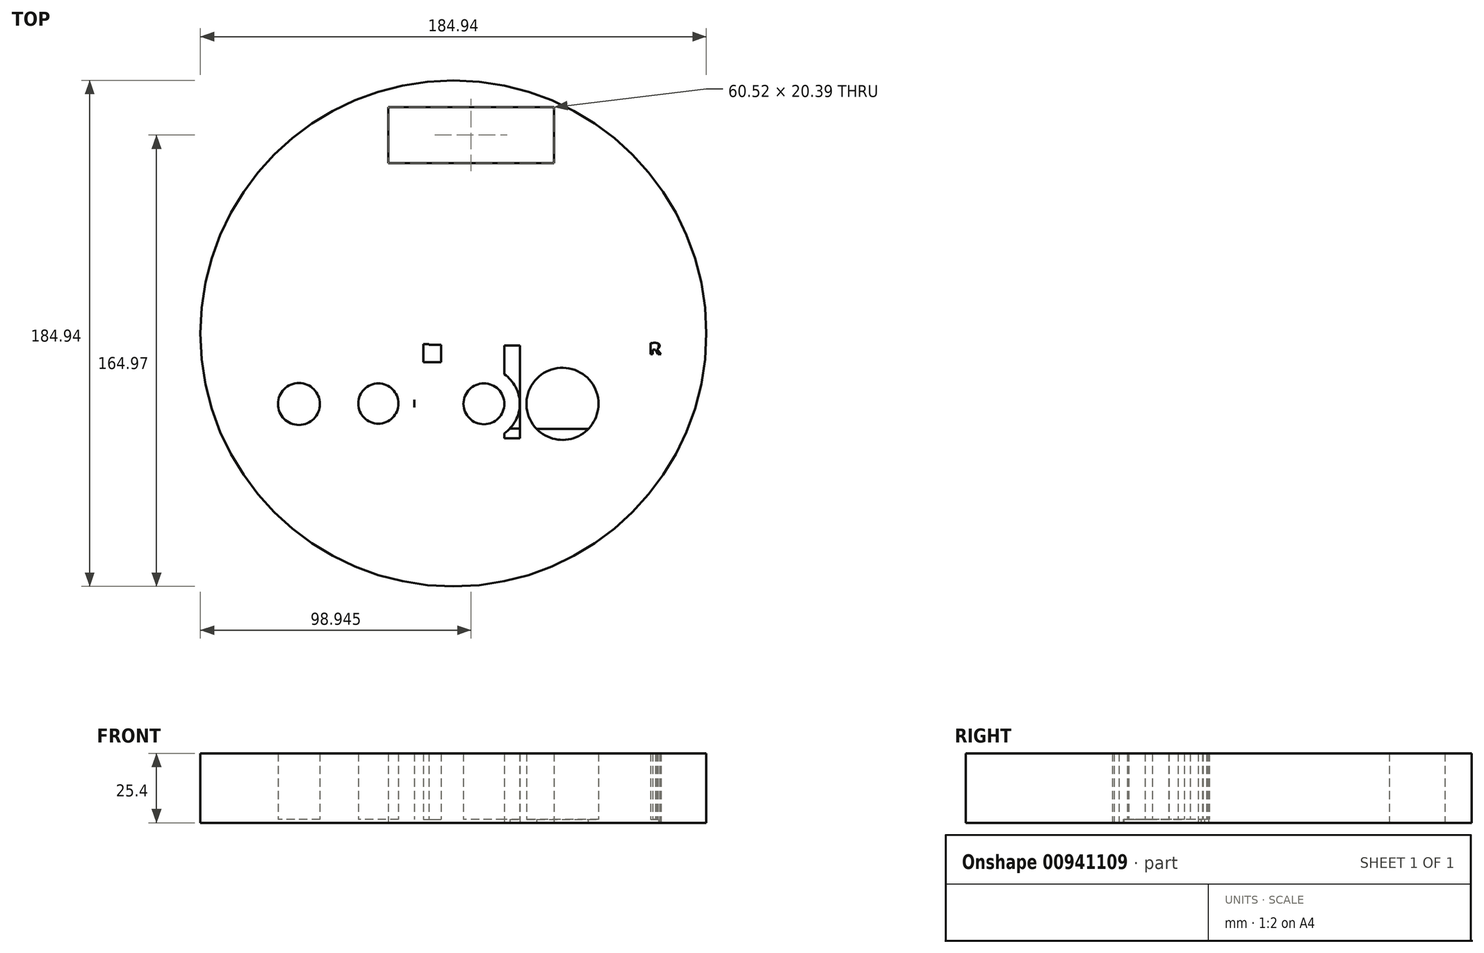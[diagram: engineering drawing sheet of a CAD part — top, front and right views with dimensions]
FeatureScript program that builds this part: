
annotation { "Feature Type Name" : "Feature", "Feature Type Description" : "" }
export const myFeature = defineFeature(function(context is Context, id is Id, definition is map)
    precondition{}
    {
        {
            var Q0;
            Q0=qCreatedBy(makeId("Top.planeOp"),FACE);
            var sketch = newSketch(context, id + "F0", { "sketchPlane" : qUnion([Q0])});
            skLineSegment(sketch, "E0", {"start": v(-100.25, 14.04) * mm, "end": v(-97.31, 8.86) * mm});
            skLineSegment(sketch, "E1", {"start": v(-97.31, 8.86) * mm, "end": v(-67.93, 8.86) * mm});
            skLineSegment(sketch, "E2", {"start": v(-68.34, 8.8) * mm, "end": v(-78.7, 26.94) * mm});
            skLineSegment(sketch, "E3", {"start": v(-78.7, 26.94) * mm, "end": v(-100.25, 14.04) * mm});
            skLineSegment(sketch, "E4", {"start": v(-74.15, 36.69) * mm, "end": v(-57.21, 8.86) * mm});
            skLineSegment(sketch, "E5", {"start": v(-57.21, 9.2) * mm, "end": v(-28.35, 8.86) * mm});
            skLineSegment(sketch, "E6", {"start": v(-28.35, 8.86) * mm, "end": v(-52.72, 50) * mm});
            skLineSegment(sketch, "E7", {"start": v(-52.72, 50) * mm, "end": v(-74.15, 36.69) * mm});
            skLineSegment(sketch, "E8", {"start": v(-26.97, 72.64) * mm, "end": v(-47.88, 60.02) * mm});
            skLineSegment(sketch, "E9", {"start": v(-47.88, 60.02) * mm, "end": v(-17.16, 9.1) * mm});
            skLineSegment(sketch, "E10", {"start": v(-17.46, 9.2) * mm, "end": v(11.36, 8.97) * mm});
            skLineSegment(sketch, "E11", {"start": v(11.36, 8.97) * mm, "end": v(-26.97, 72.64) * mm});
            skCircle(sketch, "E12", {"center": v(-102.75, -12.72) * mm, "radius": 13.23 * mm});
            skCircle(sketch, "E13", {"center": v(-102.75, -12.72) * mm, "radius": 7.67 * mm});
            skCircle(sketch, "E14", {"center": v(-73.71, -12.55) * mm, "radius": 13.19 * mm});
            skCircle(sketch, "E15", {"center": v(-73.71, -12.55) * mm, "radius": 7.35 * mm});
            skLineSegment(sketch, "E16", {"start": v(-95.55, 0.06) * mm, "end": v(-95.55, -24.87) * mm});
            skLineSegment(sketch, "E17", {"start": v(-95.55, -24.87) * mm, "end": v(-89.4, -24.87) * mm});
            skLineSegment(sketch, "E18", {"start": v(-89.4, -24.87) * mm, "end": v(-89.4, 0.06) * mm});
            skLineSegment(sketch, "E19", {"start": v(-95.55, 0.06) * mm, "end": v(-89.4, 0.06) * mm});
            skLineSegment(sketch, "E20.bottom", {"start": v(-66.38, 8.73) * mm, "end": v(-60.6, 8.73) * mm});
            skLineSegment(sketch, "E20.top", {"start": v(-66.38, -25.23) * mm, "end": v(-60.6, -25.23) * mm});
            skLineSegment(sketch, "E20.left", {"start": v(-66.38, 8.73) * mm, "end": v(-66.38, -25.23) * mm});
            skLineSegment(sketch, "E20.right", {"start": v(-60.6, 8.73) * mm, "end": v(-60.6, -25.23) * mm});
            skLineSegment(sketch, "E21.bottom", {"start": v(-57.17, 0.69) * mm, "end": v(-50.84, 0.69) * mm});
            skLineSegment(sketch, "E21.top", {"start": v(-57.17, -24.96) * mm, "end": v(-50.84, -24.96) * mm});
            skLineSegment(sketch, "E21.left", {"start": v(-57.17, 0.69) * mm, "end": v(-57.17, -24.96) * mm});
            skLineSegment(sketch, "E21.right", {"start": v(-50.84, 0.69) * mm, "end": v(-50.84, -24.96) * mm});
            skLineSegment(sketch, "E22.bottom", {"start": v(-57.21, 8.86) * mm, "end": v(-50.84, 8.86) * mm});
            skLineSegment(sketch, "E22.top", {"start": v(-57.21, 2.59) * mm, "end": v(-50.84, 2.59) * mm});
            skLineSegment(sketch, "E22.left", {"start": v(-57.21, 8.86) * mm, "end": v(-57.21, 2.59) * mm});
            skLineSegment(sketch, "E22.right", {"start": v(-50.84, 8.86) * mm, "end": v(-50.84, 2.59) * mm});
            skLineSegment(sketch, "E23.bottom", {"start": v(-57.21, 9.2) * mm, "end": v(-55.18, 9.2) * mm});
            skLineSegment(sketch, "E23.top", {"start": v(-57.21, 8.86) * mm, "end": v(-55.18, 8.86) * mm});
            skLineSegment(sketch, "E23.left", {"start": v(-57.21, 9.2) * mm, "end": v(-57.21, 8.86) * mm});
            skLineSegment(sketch, "E23.right", {"start": v(-55.18, 9.2) * mm, "end": v(-55.18, 8.86) * mm});
            skLineSegment(sketch, "E24.bottom", {"start": v(-22.01, 8.65) * mm, "end": v(-27.73, 8.65) * mm});
            skLineSegment(sketch, "E24.top", {"start": v(-22.01, -25.22) * mm, "end": v(-27.73, -25.22) * mm});
            skLineSegment(sketch, "E24.left", {"start": v(-22.01, 8.65) * mm, "end": v(-22.01, -25.22) * mm});
            skLineSegment(sketch, "E24.right", {"start": v(-27.73, 8.65) * mm, "end": v(-27.73, -25.22) * mm});
            skLineSegment(sketch, "E25.bottom", {"start": v(0.75, -0.1) * mm, "end": v(6.47, -0.1) * mm});
            skLineSegment(sketch, "E25.top", {"start": v(0.75, -25.22) * mm, "end": v(6.47, -25.22) * mm});
            skLineSegment(sketch, "E25.left", {"start": v(0.75, -0.1) * mm, "end": v(0.75, -25.22) * mm});
            skLineSegment(sketch, "E25.right", {"start": v(6.47, -0.1) * mm, "end": v(6.47, -25.22) * mm});
            skCircle(sketch, "E26", {"center": v(-35.14, -12.66) * mm, "radius": 13.1 * mm});
            skCircle(sketch, "E27", {"center": v(-35.14, -12.66) * mm, "radius": 7.46 * mm});
            skCircle(sketch, "E28", {"center": v(-6.42, -12.66) * mm, "radius": 13.17 * mm});
            skCircle(sketch, "E29", {"center": v(-6.42, -12.66) * mm, "radius": 7.45 * mm});
            skCircle(sketch, "E30", {"center": v(27.58, 7.6) * mm, "radius": 3.7 * mm});
            skFitSpline(sketch, "E31", {"points": [v(31.73, -7.2) * mm, v(10.42, -7.2) * mm], "startDerivative": vector(4.82, 29) * mm, "endDerivative": vector(0.58, -36.08) * mm});
            skFitSpline(sketch, "E32", {"points": [v(10.42, -7.2) * mm, v(25.73, -17.83) * mm], "startDerivative": vector(-2.55, -26.6) * mm, "endDerivative": vector(-4.22, -9.84) * mm});
            skFitSpline(sketch, "E33", {"points": [v(25.73, -17.83) * mm, v(16.12, -16.9) * mm], "startDerivative": vector(1.4, -10.54) * mm, "endDerivative": vector(-2.28, 16.16) * mm});
            skLineSegment(sketch, "E34.bottom", {"start": v(25.74, 9.6) * mm, "end": v(26.5, 9.6) * mm});
            skLineSegment(sketch, "E34.top", {"start": v(25.74, 5.52) * mm, "end": v(26.5, 5.52) * mm});
            skLineSegment(sketch, "E34.left", {"start": v(25.74, 9.6) * mm, "end": v(25.74, 5.52) * mm});
            skLineSegment(sketch, "E34.right", {"start": v(26.5, 9.6) * mm, "end": v(26.5, 5.52) * mm});
            skFitSpline(sketch, "E35", {"points": [v(9.56, -17.02) * mm, v(32.29, -16.9) * mm], "startDerivative": vector(0.9, -39.05) * mm, "endDerivative": vector(-5.97, 28.7) * mm});
            skLineSegment(sketch, "E36", {"start": v(9.56, -17.02) * mm, "end": v(16.12, -16.9) * mm});
            skLineSegment(sketch, "E37", {"start": v(31.73, -7.2) * mm, "end": v(25.33, -7.2) * mm});
            skFitSpline(sketch, "E38", {"points": [v(32.29, -16.9) * mm, v(16.92, -5.43) * mm], "startDerivative": vector(5.97, 25.82) * mm, "endDerivative": vector(6.24, 16.29) * mm});
            skFitSpline(sketch, "E39", {"points": [v(16.92, -5.43) * mm, v(25.33, -7.2) * mm], "startDerivative": vector(9.22, 8.16) * mm, "endDerivative": vector(0.27, -10.53) * mm});
            skFitSpline(sketch, "E40", {"points": [v(26.5, 9.6) * mm, v(28.05, 7.33) * mm], "startDerivative": vector(10, 1.03) * mm, "endDerivative": vector(-4.52, -1.9) * mm});
            skFitSpline(sketch, "E41", {"points": [v(27.53, 8.88) * mm, v(27.53, 7.97) * mm], "startDerivative": vector(3.44, 0.33) * mm, "endDerivative": vector(-3.2, 0.15) * mm});
            skLineSegment(sketch, "E42", {"start": v(26.5, 8.85) * mm, "end": v(27.53, 8.88) * mm});
            skLineSegment(sketch, "E43", {"start": v(27.53, 7.97) * mm, "end": v(26.5, 7.97) * mm});
            skLineSegment(sketch, "E44", {"start": v(28.4, 5.5) * mm, "end": v(29.57, 5.5) * mm});
            skLineSegment(sketch, "E45", {"start": v(28.05, 7.33) * mm, "end": v(29.57, 5.5) * mm});
            skLineSegment(sketch, "E46", {"start": v(28.4, 5.5) * mm, "end": v(27.53, 7.1) * mm});
            skLineSegment(sketch, "E47", {"start": v(27.53, 7.1) * mm, "end": v(26.5, 7.1) * mm});
            skCircle(sketch, "E48", {"center": v(-46.3, 13.08) * mm, "radius": 92.47 * mm});
            skLineSegment(sketch, "E49.bottom", {"start": v(-70.09, 95.78) * mm, "end": v(-9.56, 95.78) * mm});
            skLineSegment(sketch, "E49.top", {"start": v(-70.09, 75.38) * mm, "end": v(-9.56, 75.38) * mm});
            skLineSegment(sketch, "E49.left", {"start": v(-70.09, 95.78) * mm, "end": v(-70.09, 75.38) * mm});
            skLineSegment(sketch, "E49.right", {"start": v(-9.56, 95.78) * mm, "end": v(-9.56, 75.38) * mm});
            skCircle(sketch, "E50", {"center": v(-42.25, 85.74) * mm, "radius": 9.74 * mm});
            skSolve(sketch);
        }
        {
            var Q0;
            {var subQ0=sQuery(id+"F0.wireOp",EDGE,"E16");var subQ1=sQuery(id+"F0.wireOp",EDGE,"E12");var subQ2=makeQuery(id+"F0.imprint","INTERSECT",VERTEX,{"disambiguationData":[OD(0.0)],"derivedFrom":[subQ1,subQ0]});Q0=makeQuery(id+"F0.imprint","IMPRINT",FACE,{"disambiguationData":[TD([[makeQuery(id+"F0.imprint","IMPRINT",EDGE,{"disambiguationData":[TD([[subQ2,-1.0]])],"derivedFrom":subQ1}),1.0]])]});}
            var Q1;
            {var subQ0=sQuery(id+"F0.wireOp",EDGE,"E16");var subQ1=sQuery(id+"F0.wireOp",EDGE,"E12");var subQ2=makeQuery(id+"F0.imprint","INTERSECT",VERTEX,{"disambiguationData":[OD(0.0)],"derivedFrom":[subQ1,subQ0]});Q1=makeQuery(id+"F0.imprint","IMPRINT",FACE,{"disambiguationData":[TD([[makeQuery(id+"F0.imprint","IMPRINT",EDGE,{"disambiguationData":[TD([[subQ2,1.0]])],"derivedFrom":subQ1}),1.0]])]});}
            var Q2;
            {var subQ0=sQuery(id+"F0.wireOp",EDGE,"E17");Q2=makeQuery(id+"F0.imprint","IMPRINT",FACE,{"disambiguationData":[TD([[makeQuery(id+"F0.imprint","IMPRINT",EDGE,{"derivedFrom":subQ0}),1.0]])]});}
            var Q3;
            {var subQ0=sQuery(id+"F0.wireOp",EDGE,"E20.left");var subQ1=sQuery(id+"F0.wireOp",EDGE,"E14");var subQ2=makeQuery(id+"F0.imprint","INTERSECT",VERTEX,{"disambiguationData":[OD(0.0)],"derivedFrom":[subQ1,subQ0]});Q3=makeQuery(id+"F0.imprint","IMPRINT",FACE,{"disambiguationData":[TD([[makeQuery(id+"F0.imprint","IMPRINT",EDGE,{"disambiguationData":[TD([[subQ2,-1.0]])],"derivedFrom":subQ1}),1.0]])]});}
            var Q4;
            {var subQ5=sQuery(id+"F0.wireOp",EDGE,"E20.top");Q4=makeQuery(id+"F0.imprint","IMPRINT",FACE,{"disambiguationData":[TD([[makeQuery(id+"F0.imprint","IMPRINT",EDGE,{"derivedFrom":subQ5}),1.0]])]});}
            var Q5;
            {var subQ0=sQuery(id+"F0.wireOp",EDGE,"E20.left");var subQ1=sQuery(id+"F0.wireOp",EDGE,"E14");var subQ2=makeQuery(id+"F0.imprint","INTERSECT",VERTEX,{"disambiguationData":[OD(0.0)],"derivedFrom":[subQ1,subQ0]});Q5=makeQuery(id+"F0.imprint","IMPRINT",FACE,{"disambiguationData":[TD([[makeQuery(id+"F0.imprint","IMPRINT",EDGE,{"disambiguationData":[TD([[subQ2,1.0]])],"derivedFrom":subQ1}),1.0]])]});}
            var Q6;
            {var subQ5=sQuery(id+"F0.wireOp",EDGE,"E20.bottom");Q6=makeQuery(id+"F0.imprint","IMPRINT",FACE,{"disambiguationData":[TD([[makeQuery(id+"F0.imprint","IMPRINT",EDGE,{"derivedFrom":subQ5}),-1.0]])]});}
            var Q7;
            Q7=makeQuery(id+"F0.imprint","IMPRINT",FACE,{"disambiguationData":[TD([[makeQuery(id+"F0.imprint","IMPRINT",EDGE,{"derivedFrom":sQuery(id+"F0.wireOp",EDGE,"E21.bottom")}),-1.0]])]});
            var Q8;
            {var subQ0=sQuery(id+"F0.wireOp",EDGE,"E26");var subQ1=sQuery(id+"F0.wireOp",EDGE,"E24.right");var subQ2=makeQuery(id+"F0.imprint","INTERSECT",VERTEX,{"disambiguationData":[OD(0.0)],"derivedFrom":[subQ1,subQ0]});Q8=makeQuery(id+"F0.imprint","IMPRINT",FACE,{"disambiguationData":[TD([[makeQuery(id+"F0.imprint","IMPRINT",EDGE,{"disambiguationData":[TD([[subQ2,-1.0]])],"derivedFrom":subQ1}),-1.0]])]});}
            var Q9;
            {var subQ0=sQuery(id+"F0.wireOp",EDGE,"E26");var subQ1=sQuery(id+"F0.wireOp",EDGE,"E24.right");var subQ2=makeQuery(id+"F0.imprint","INTERSECT",VERTEX,{"disambiguationData":[OD(0.0)],"derivedFrom":[subQ1,subQ0]});Q9=makeQuery(id+"F0.imprint","IMPRINT",FACE,{"disambiguationData":[TD([[makeQuery(id+"F0.imprint","IMPRINT",EDGE,{"disambiguationData":[TD([[subQ2,-1.0]])],"derivedFrom":subQ1}),1.0]])]});}
            var Q10;
            {var subQ0=sQuery(id+"F0.wireOp",EDGE,"E28");var subQ1=sQuery(id+"F0.wireOp",EDGE,"E25.left");var subQ2=makeQuery(id+"F0.imprint","INTERSECT",VERTEX,{"disambiguationData":[OD(0.0)],"derivedFrom":[subQ1,subQ0]});Q10=makeQuery(id+"F0.imprint","IMPRINT",FACE,{"disambiguationData":[TD([[makeQuery(id+"F0.imprint","IMPRINT",EDGE,{"disambiguationData":[TD([[subQ2,-1.0]])],"derivedFrom":subQ1}),-1.0]])]});}
            var Q11;
            {var subQ0=sQuery(id+"F0.wireOp",EDGE,"E28");var subQ1=sQuery(id+"F0.wireOp",EDGE,"E25.left");var subQ2=makeQuery(id+"F0.imprint","INTERSECT",VERTEX,{"disambiguationData":[OD(0.0)],"derivedFrom":[subQ1,subQ0]});Q11=makeQuery(id+"F0.imprint","IMPRINT",FACE,{"disambiguationData":[TD([[makeQuery(id+"F0.imprint","IMPRINT",EDGE,{"disambiguationData":[TD([[subQ2,-1.0]])],"derivedFrom":subQ1}),1.0]])]});}
            var Q12;
            {var subQ0=sQuery(id+"F0.wireOp",EDGE,"E25.bottom");Q12=makeQuery(id+"F0.imprint","IMPRINT",FACE,{"disambiguationData":[TD([[makeQuery(id+"F0.imprint","IMPRINT",EDGE,{"derivedFrom":subQ0}),-1.0]])]});}
            var Q13;
            {var subQ0=sQuery(id+"F0.wireOp",EDGE,"E25.top");Q13=makeQuery(id+"F0.imprint","IMPRINT",FACE,{"disambiguationData":[TD([[makeQuery(id+"F0.imprint","IMPRINT",EDGE,{"derivedFrom":subQ0}),1.0]])]});}
            var Q14;
            {var subQ0=sQuery(id+"F0.wireOp",EDGE,"E8");Q14=makeQuery(id+"F0.imprint","IMPRINT",FACE,{"disambiguationData":[TD([[makeQuery(id+"F0.imprint","IMPRINT",EDGE,{"derivedFrom":subQ0}),1.0]])]});}
            var Q15;
            {var subQ0=sQuery(id+"F0.wireOp",EDGE,"E0");Q15=makeQuery(id+"F0.imprint","IMPRINT",FACE,{"disambiguationData":[TD([[makeQuery(id+"F0.imprint","IMPRINT",EDGE,{"derivedFrom":subQ0}),1.0]])]});}
            var Q16;
            Q16=makeQuery(id+"F0.imprint","IMPRINT",FACE,{"disambiguationData":[TD([[makeQuery(id+"F0.imprint","IMPRINT",EDGE,{"derivedFrom":sQuery(id+"F0.wireOp",EDGE,"E4")}),1.0]])]});
            var Q17;
            Q17=makeQuery(id+"F0.imprint","IMPRINT",FACE,{"disambiguationData":[TD([[makeQuery(id+"F0.imprint","IMPRINT",EDGE,{"derivedFrom":sQuery(id+"F0.wireOp",EDGE,"E31")}),1.0]])]});
            var Q18;
            Q18=makeQuery(id+"F0.imprint","IMPRINT",FACE,{"disambiguationData":[TD([[makeQuery(id+"F0.imprint","IMPRINT",EDGE,{"derivedFrom":sQuery(id+"F0.wireOp",EDGE,"E30")}),1.0]])]});
            extrude(context, id + "F1", {"entities" : qUnion([Q0, Q1, Q2, Q3, Q4, Q5, Q6, Q7, Q8, Q9, Q10, Q11, Q12, Q13, Q14, Q15, Q16, Q17, Q18]), "depth" : 25.4 * mm, "offsetDistance" : 25.4 * mm});
        }
        {
            var Q0;
            Q0=qCreatedBy(makeId("Top.planeOp"),FACE);
            var sketch = newSketch(context, id + "F2", { "sketchPlane" : qUnion([Q0])});
            skLineSegment(sketch, "E51.bottom", {"start": v(-17.24, 55.88) * mm, "end": v(-111.76, 55.88) * mm});
            skLineSegment(sketch, "E51.top", {"start": v(-17.24, -21.7) * mm, "end": v(-111.76, -21.7) * mm});
            skLineSegment(sketch, "E51.left", {"start": v(-17.24, 55.88) * mm, "end": v(-17.24, -21.7) * mm});
            skLineSegment(sketch, "E51.right", {"start": v(-111.76, 55.88) * mm, "end": v(-111.76, -21.7) * mm});
            skLineSegment(sketch, "E52.bottom", {"start": v(-17.24, 55.88) * mm, "end": v(28.71, 55.88) * mm});
            skLineSegment(sketch, "E52.top", {"start": v(-17.24, -21.87) * mm, "end": v(28.71, -21.87) * mm});
            skLineSegment(sketch, "E52.left", {"start": v(-17.24, 55.88) * mm, "end": v(-17.24, -21.87) * mm});
            skLineSegment(sketch, "E52.right", {"start": v(28.71, 55.88) * mm, "end": v(28.71, -21.87) * mm});
            skSolve(sketch);
        }
        {
            var Q0;
            Q0=makeQuery(id+"F2.imprint","IMPRINT",FACE,{"disambiguationData":[TD([[makeQuery(id+"F2.imprint","IMPRINT",EDGE,{"derivedFrom":sQuery(id+"F2.wireOp",EDGE,"E51.bottom")}),1.0]])]});
            var Q1;
            Q1=makeQuery(id+"F2.imprint","IMPRINT",FACE,{"disambiguationData":[TD([[makeQuery(id+"F2.imprint","IMPRINT",EDGE,{"derivedFrom":sQuery(id+"F2.wireOp",EDGE,"E51.left")}),1.0]])]});
            extrude(context, id + "F3", {"entities" : qUnion([Q0, Q1]), "operationType" : NewBodyOperationType.ADD, "depth" : 1.27 * mm, "offsetDistance" : 25.4 * mm});
        }
    });
